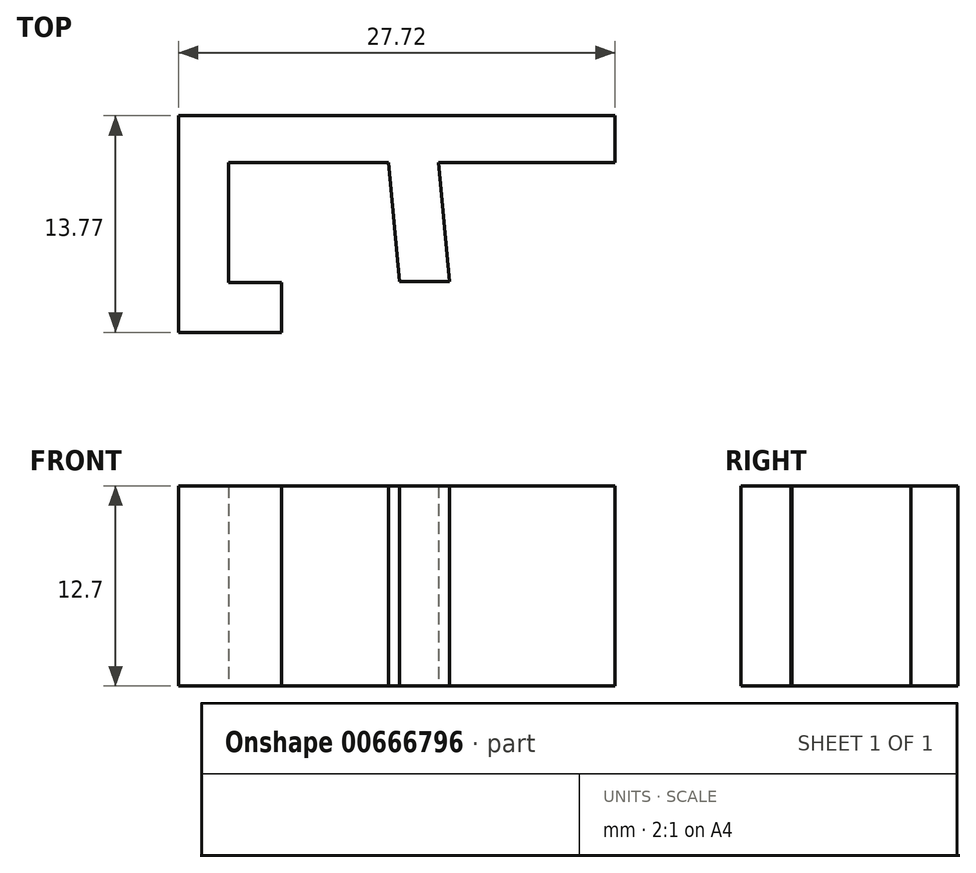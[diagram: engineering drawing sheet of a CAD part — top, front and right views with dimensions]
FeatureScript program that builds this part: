
annotation { "Feature Type Name" : "Feature", "Feature Type Description" : "" }
export const myFeature = defineFeature(function(context is Context, id is Id, definition is map)
    precondition{}
    {
        {
            var Q0;
            Q0=qCreatedBy(makeId("Top.planeOp"),FACE);
            var sketch = newSketch(context, id + "F0", { "sketchPlane" : qUnion([Q0])});
            skLineSegment(sketch, "E0.bottom", {"start": v(-13.34, 2.98) * mm, "end": v(-10.16, 2.98) * mm});
            skLineSegment(sketch, "E0.top", {"start": v(-13.34, -10.8) * mm, "end": v(-10.16, -10.8) * mm});
            skLineSegment(sketch, "E0.left", {"start": v(-13.34, 2.98) * mm, "end": v(-13.34, -10.8) * mm});
            skLineSegment(sketch, "E0.right", {"start": v(-10.16, 2.98) * mm, "end": v(-10.16, -10.8) * mm});
            skLineSegment(sketch, "E1.bottom", {"start": v(-6.79, -7.62) * mm, "end": v(-13.34, -7.62) * mm});
            skLineSegment(sketch, "E1.top", {"start": v(-6.79, -10.8) * mm, "end": v(-13.34, -10.8) * mm});
            skLineSegment(sketch, "E1.left", {"start": v(-6.79, -7.62) * mm, "end": v(-6.79, -10.8) * mm});
            skLineSegment(sketch, "E1.right", {"start": v(-13.34, -7.62) * mm, "end": v(-13.34, -10.8) * mm});
            skLineSegment(sketch, "E2.bottom", {"start": v(-13.34, 2.98) * mm, "end": v(2.9, 2.98) * mm});
            skLineSegment(sketch, "E2.top", {"start": v(-13.34, 0) * mm, "end": v(3.18, 0) * mm});
            skLineSegment(sketch, "E2.left", {"start": v(-13.34, 2.98) * mm, "end": v(-13.34, 0) * mm});
            skLineSegment(sketch, "E2.right", {"start": v(2.9, 2.98) * mm, "end": v(3.18, 0) * mm});
            skLineSegment(sketch, "E3.bottom", {"start": v(1.27, -10.16) * mm, "end": v(4.44, -10.16) * mm});
            skLineSegment(sketch, "E3.top", {"start": v(1.27, -13.34) * mm, "end": v(4.44, -13.34) * mm});
            skLineSegment(sketch, "E3.left", {"start": v(1.27, -10.16) * mm, "end": v(1.27, -13.34) * mm});
            skLineSegment(sketch, "E3.right", {"start": v(4.44, -10.16) * mm, "end": v(4.44, -13.34) * mm});
            skLineSegment(sketch, "E4", {"start": v(0, 0) * mm, "end": v(1.27, -13.34) * mm});
            skLineSegment(sketch, "E5", {"start": v(3.18, 0) * mm, "end": v(4.44, -13.34) * mm});
            skLineSegment(sketch, "E6.bottom", {"start": v(0, 2.98) * mm, "end": v(14.4, 2.98) * mm});
            skLineSegment(sketch, "E6.top", {"start": v(0, 0) * mm, "end": v(14.4, 0) * mm});
            skLineSegment(sketch, "E6.left", {"start": v(0, 2.98) * mm, "end": v(0, 0) * mm});
            skLineSegment(sketch, "E6.right", {"start": v(14.4, 2.98) * mm, "end": v(14.4, 0) * mm});
            skSolve(sketch);
        }
        {
            var Q0;
            Q0=qSketchRegion(id+"F0",true);
            extrude(context, id + "F1", {"entities" : qUnion([Q0]), "depth" : 12.7 * mm, "offsetDistance" : 25.4 * mm});
        }
        {
            var Q0;
            Q0=qCreatedBy(makeId("Top.planeOp"),FACE);
            var sketch = newSketch(context, id + "F2", { "sketchPlane" : qUnion([Q0])});
            skLineSegment(sketch, "E7.bottom", {"start": v(6.88, -7.56) * mm, "end": v(0, -7.56) * mm});
            skLineSegment(sketch, "E7.top", {"start": v(6.88, -16.42) * mm, "end": v(0, -16.42) * mm});
            skLineSegment(sketch, "E7.left", {"start": v(6.88, -7.56) * mm, "end": v(6.88, -16.42) * mm});
            skLineSegment(sketch, "E7.right", {"start": v(0, -7.56) * mm, "end": v(0, -16.42) * mm});
            skSolve(sketch);
        }
        {
            var Q0;
            Q0 = qSketchRegion(id + "F2", true);
            extrude(context, id + "F3", {"entities" : qUnion([Q0]), "operationType" : NewBodyOperationType.REMOVE, "depth" : 25.4 * mm, "offsetDistance" : 25.4 * mm});
        }
    });
